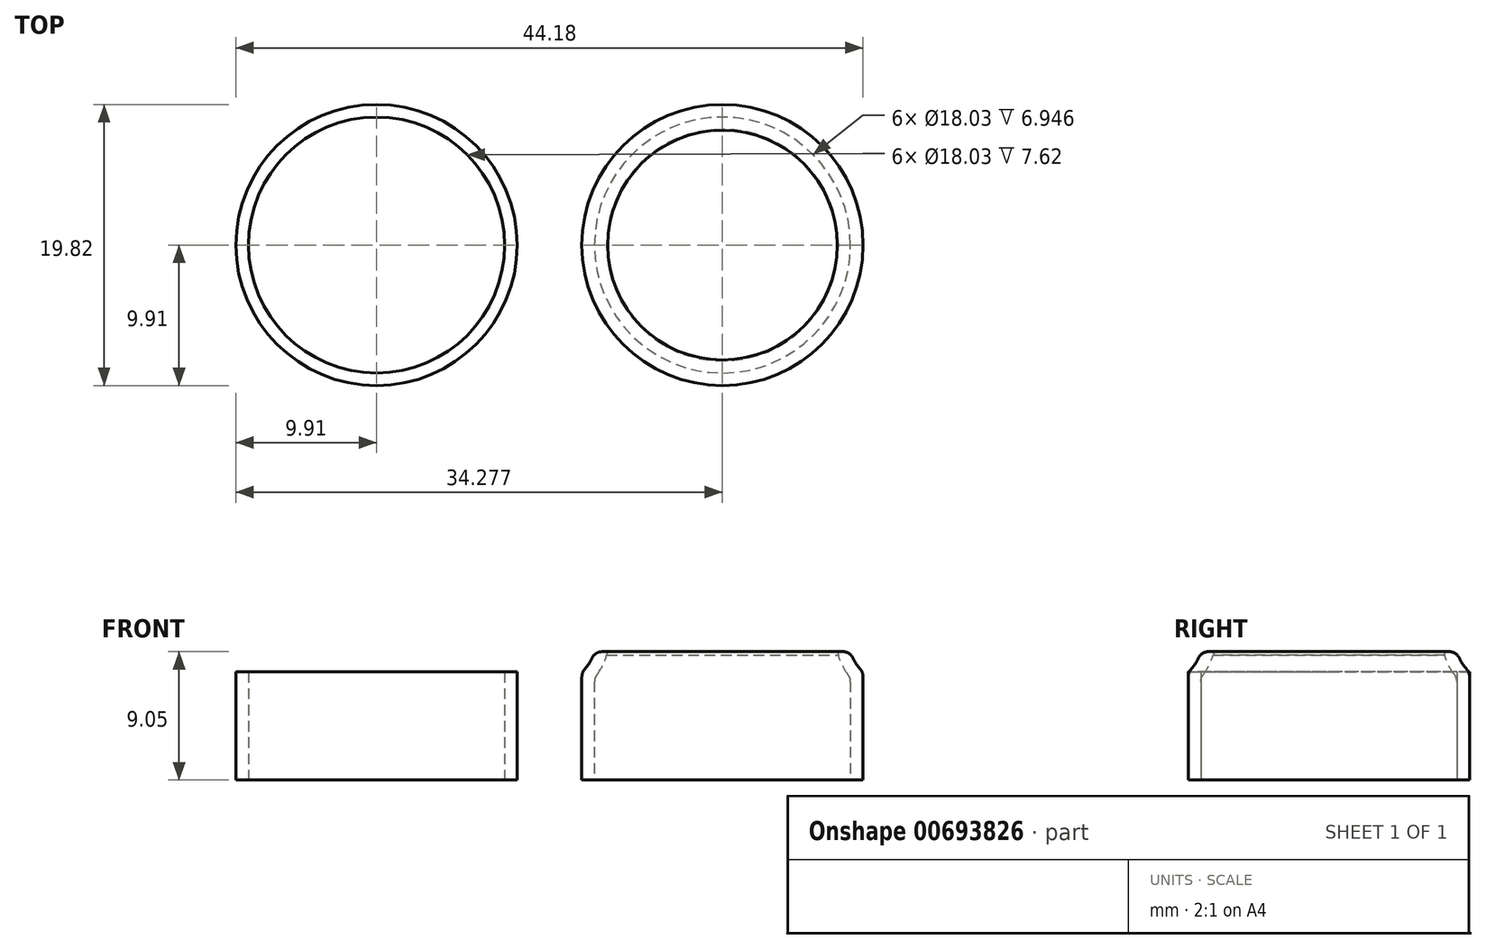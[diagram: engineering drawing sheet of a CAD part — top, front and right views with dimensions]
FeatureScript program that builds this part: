
annotation { "Feature Type Name" : "Feature", "Feature Type Description" : "" }
export const myFeature = defineFeature(function(context is Context, id is Id, definition is map)
    precondition{}
    {
        {
            var Q0;
            Q0=qCreatedBy(makeId("Top.planeOp"),FACE);
            var sketch = newSketch(context, id + "F0", { "sketchPlane" : qUnion([Q0])});
            skCircle(sketch, "E0", {"center": v(0, 0) * mm, "radius": 9.9 * mm});
            skCircle(sketch, "E1.0", {"center": v(0, 0) * mm, "radius": 9.02 * mm});
            skSolve(sketch);
        }
        {
            var Q0;
            Q0 = qSketchRegion(id + "F0", true);
            extrude(context, id + "F1", {"entities" : qUnion([Q0]), "depth" : 7.62 * mm, "offsetDistance" : 25.4 * mm});
        }
        {
            var Q0;
            Q0=qCreatedBy(makeId("Front.planeOp"),FACE);
            var sketch = newSketch(context, id + "F2", { "sketchPlane" : qUnion([Q0])});
            skLineSegment(sketch, "E2", {"start": v(14.46, 0) * mm, "end": v(14.46, 7.62) * mm});
            skFitSpline(sketch, "E3", {"points": [v(14.46, 7.62) * mm, v(15.35, 9.05) * mm], "startDerivative": vector(1.36, 1.13) * mm, "endDerivative": vector(0.34, 1.24) * mm});
            skFitSpline(sketch, "E4.0", {"points": [v(15.03, 6.94) * mm, v(15.2, 7.08) * mm, v(15.49, 7.38) * mm, v(15.82, 7.87) * mm, v(16.06, 8.36) * mm, v(16.17, 8.66) * mm, v(16.2, 8.81) * mm]});
            skLineSegment(sketch, "E4.1", {"start": v(15.35, 0) * mm, "end": v(15.35, 7.25) * mm});
            skLineSegment(sketch, "E5", {"start": v(15.35, 9.05) * mm, "end": v(16.27, 9.05) * mm});
            skLineSegment(sketch, "E6", {"start": v(16.2, 8.81) * mm, "end": v(16.27, 9.05) * mm});
            skLineSegment(sketch, "E7", {"start": v(14.46, 0) * mm, "end": v(15.35, 0) * mm});
            skLineSegment(sketch, "E8.0", {"start": v(24.37, 0) * mm, "end": v(24.37, 7.62) * mm, "construction": true});
            skSolve(sketch);
        }
        {
            var Q0;
            Q0 = qSketchRegion(id + "F2", true);
            var Q1;
            Q1=sQuery(id+"F2.wireOp",EDGE,"E8.0");
            revolve(context, id + "F3", {"entities" : qUnion([Q0]), "axis" : qUnion([Q1]), "revolveType" : RevolveType.FULL});
        }
        {
            var Q0;
            Q0=makeQuery(id+"F3.opRevolve","SWEPT_EDGE",EDGE,{"disambiguationData":[OSD([sQuery(id+"F2.wireOp",EDGE,"E2"),sQuery(id+"F2.wireOp",EDGE,"E3")])]});
            var Q1;
            Q1=makeQuery(id+"F3.opRevolve","SWEPT_EDGE",EDGE,{"disambiguationData":[OSD([sQuery(id+"F2.wireOp",EDGE,"E3"),sQuery(id+"F2.wireOp",EDGE,"E5")])]});
            var Q2;
            Q2=makeQuery(id+"F3.opRevolve","SWEPT_EDGE",EDGE,{"disambiguationData":[OSD([sQuery(id+"F2.wireOp",EDGE,"E4.0"),sQuery(id+"F2.wireOp",EDGE,"E4.1")])]});
            fillet(context, id + "F4", {"entities" : qUnion([Q0, Q1, Q2]), "radius" : 0.76 * mm, "tangentPropagation" : true, "allowEdgeOverflow" : false});
        }
    });
